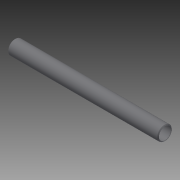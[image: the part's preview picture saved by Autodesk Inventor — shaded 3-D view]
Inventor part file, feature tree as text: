
AUTODESK INVENTOR PART (.ipt)
format: ipt  version: 2013 (Build 170138000, 138)  size: 124,928 bytes
history: native  units: in
note: dims shown in document units (in); Inventor stores cm internally (conversion verified against a paired STEP export)
features: other x42, revolve x1, sketch x1
ambient origin geometry x8: Origin, YZ Plane, XZ Plane, XY Plane, X Axis, Y Axis, Z Axis, Center Point
bodies: Solid1 (feature_tree)
feature tree (44):
  revolve  "Revolution1"  [1 undecoded]
  other  "tube_front_XY"
  other  "tube_front_YZ"
  other  "tube_front_ZX"
  other  "tube_front_X"
  other  "tube_front_Y"
  other  "tube_front_Z"
  other  "tube_front_Center"
  other  "tube_rear_XY"
  other  "tube_rear_YZ"
  other  "tube_rear_ZX"
  other  "tube_rear_X"
  other  "tube_rear_Y"
  other  "tube_rear_Z"
  other  "tube_rear_Center"
  other  "cp1_XY"
  other  "cp1_YZ"
  other  "cp1_ZX"
  other  "cp1_X"
  other  "cp1_Y"
  other  "cp1_Z"
  other  "cp1_Center"
  other  "cp2_XY"
  other  "cp2_YZ"
  other  "cp2_ZX"
  other  "cp2_X"
  other  "cp2_Y"
  other  "cp2_Z"
  other  "cp2_Center"
  other  "cp3_XY"
  other  "cp3_YZ"
  other  "cp3_ZX"
  other  "cp3_X"
  other  "cp3_Y"
  other  "cp3_Z"
  other  "cp3_Center"
  other  "cp4_XY"
  other  "cp4_YZ"
  other  "cp4_ZX"
  other  "cp4_X"
  other  "cp4_Y"
  other  "cp4_Z"
  other  "cp4_Center"
  sketch  "Sketch_1"  dims[d0=360.0deg]
note: 1 required parameter value undecoded (feature->parameter linkage not recoverable at this tier; creation-order binding heuristic only, values carry confidence <= 0.55)
